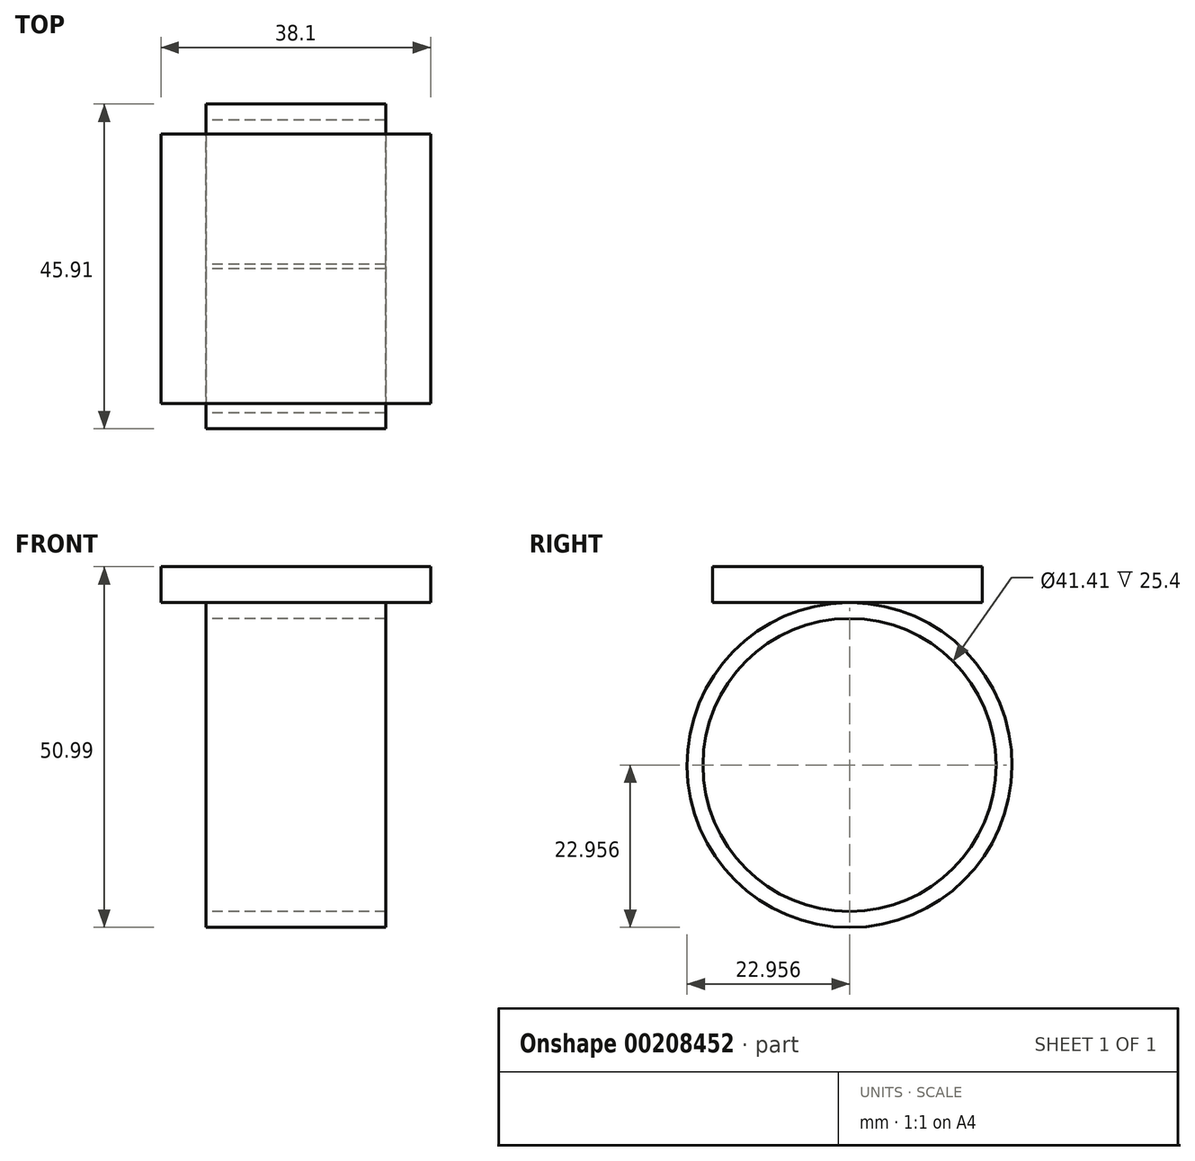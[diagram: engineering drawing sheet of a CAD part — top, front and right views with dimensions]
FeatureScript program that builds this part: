
annotation { "Feature Type Name" : "Feature", "Feature Type Description" : "" }
export const myFeature = defineFeature(function(context is Context, id is Id, definition is map)
    precondition{}
    {
        {
            var Q0;
            Q0=qCreatedBy(makeId("Top.planeOp"),FACE);
            var sketch = newSketch(context, id + "F0", { "sketchPlane" : qUnion([Q0])});
            skLineSegment(sketch, "E0.bottom", {"start": v(19.05, 19.05) * mm, "end": v(-19.05, 19.05) * mm});
            skLineSegment(sketch, "E0.top", {"start": v(19.05, -19.05) * mm, "end": v(-19.05, -19.05) * mm});
            skLineSegment(sketch, "E0.left", {"start": v(19.05, 19.05) * mm, "end": v(19.05, -19.05) * mm});
            skLineSegment(sketch, "E0.right", {"start": v(-19.05, 19.05) * mm, "end": v(-19.05, -19.05) * mm});
            skPoint(sketch, "E0.middle", {"position": v(0, 0) * mm});
            skSolve(sketch);
        }
        {
            var Q0;
            Q0=makeQuery(id+"F0.imprint","IMPRINT",FACE,{"disambiguationData":[TD([[makeQuery(id+"F0.imprint","IMPRINT",EDGE,{"derivedFrom":sQuery(id+"F0.wireOp",EDGE,"E0.bottom")}),1.0]])]});
            extrude(context, id + "F1", {"entities" : qUnion([Q0]), "depth" : 5.08 * mm});
        }
        {
            var Q0;
            Q0=qCreatedBy(makeId("Right.planeOp"),FACE);
            var sketch = newSketch(context, id + "F2", { "sketchPlane" : qUnion([Q0])});
            skCircle(sketch, "E1", {"center": v(0.32, -22.95) * mm, "radius": 22.96 * mm});
            skPoint(sketch, "E1.first.point", {"position": v(0, 0) * mm});
            skPoint(sketch, "E1.second.point", {"position": v(0, -45.9) * mm});
            skPoint(sketch, "E1.third.point", {"position": v(23.24, -24.18) * mm});
            skCircle(sketch, "E2", {"center": v(0.32, -22.95) * mm, "radius": 20.7 * mm});
            skSolve(sketch);
        }
        {
            var Q0;
            Q0=qSketchRegion(id+"F2",true);
            extrude(context, id + "F3", {"entities" : qUnion([Q0]), "operationType" : NewBodyOperationType.ADD, "endBound" : BoundingType.SYMMETRIC, "depth" : 25.4 * mm});
        }
    });
